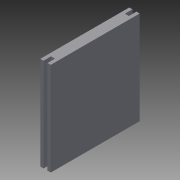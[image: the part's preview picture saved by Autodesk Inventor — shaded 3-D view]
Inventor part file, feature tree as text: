
AUTODESK INVENTOR PART (.ipt)
format: ipt  version: 2014 (Build 180170000, 170)  size: 82,944 bytes
history: native  units: in
note: dims shown in document units (in); Inventor stores cm internally (conversion verified against a paired STEP export)
features: extrude x1, sketch x1
ambient origin geometry x8: Origin, YZ Plane, XZ Plane, XY Plane, X Axis, Y Axis, Z Axis, Center Point
bodies: Solid1 (feature_tree)
feature tree (2):
  extrude  "Extrusion1"  Depth=2.48in
  sketch  "Sketch1"  dims[d0=0.29in d1=2.48in d2=0.09in d3=0.09in d4=0.21in d5=0.09in d6=0.09in d7=0.21in d8=0.21in d9=0.21in d10=0.21in d11=2.6in d12=0.0in]
